# Revit family: LHBA
name_source: partatom
category: Lighting Fixtures
units: mm (PartAtom-declared; Revit-internal decimal feet)

## family parameters
Always vertical = Yes
Cut with Voids When Loaded = No
Host = Ceiling
Light Source = Yes
OmniClass Number = 23.80.70.11.14.11
OmniClass Title = Downlights
Part Type = Normal
Room Calculation Point = No
Round Connector Dimension = Use Diameter
Shared = No

## types (5) — shared parameters
Assembly Code = D5020200
Color Filter = 16777215
Description = LED Pendant Mount High Bay
Dimming Lamp Color Temperature Shift = <None>
Emit Shape Visible in Rendering = No
Emit from Rectangle Length = 2' - 0"
Emit from Rectangle Width = 2' - 0"
Height = 0' - 4 1/2"
Housing Finish = Metal - Viscor - White
Lamp = LED
Length = 2' - 0"
Lens Finish = Polycarbonate - Viscor - White Translucent
Manufacturer = VISIONEERING by VISCOR
Model = LHBA
Tilt Angle = 90.00°
URL = https://www.viscor.com
Voltage = 120 V
Width = 2' - 0"

## per-type parameters (varying)
| type | Apparent Load | Lamp Wattage | Photometric Web File |
| LHBA2x2-LED840K100LUNV-P73 | 79 VA | 79 VA | LHBA2x2-LED840K100LUNV-P73.ies |
| LHBA2x2-LED840K120LUNV-P73 | 92 VA | 92 VA | LHBA2x2-LED840K120LUNV-P73-G0579.IES |
| LHBA2x2-LED840K150LUNV-P73 | 119 VA | 119 VA | LHBA2x2-LED840K150LUNV-P73-G001692.IES |
| LHBA2x2-LED840K200LUNV-P73 | 156 VA | 156 VA | LHBA2x2-LED840K200LUNV-P73.ies |
| LHBA2x2-LED840K240LUNV-P73 | 186 VA | 186 VA | LHBA2x2-LED840K240LUNV-P73-G001727.IES |

## geometry (parser evidence)
native form markers: Sweep x2
no freeform markers — native parametric forms only
